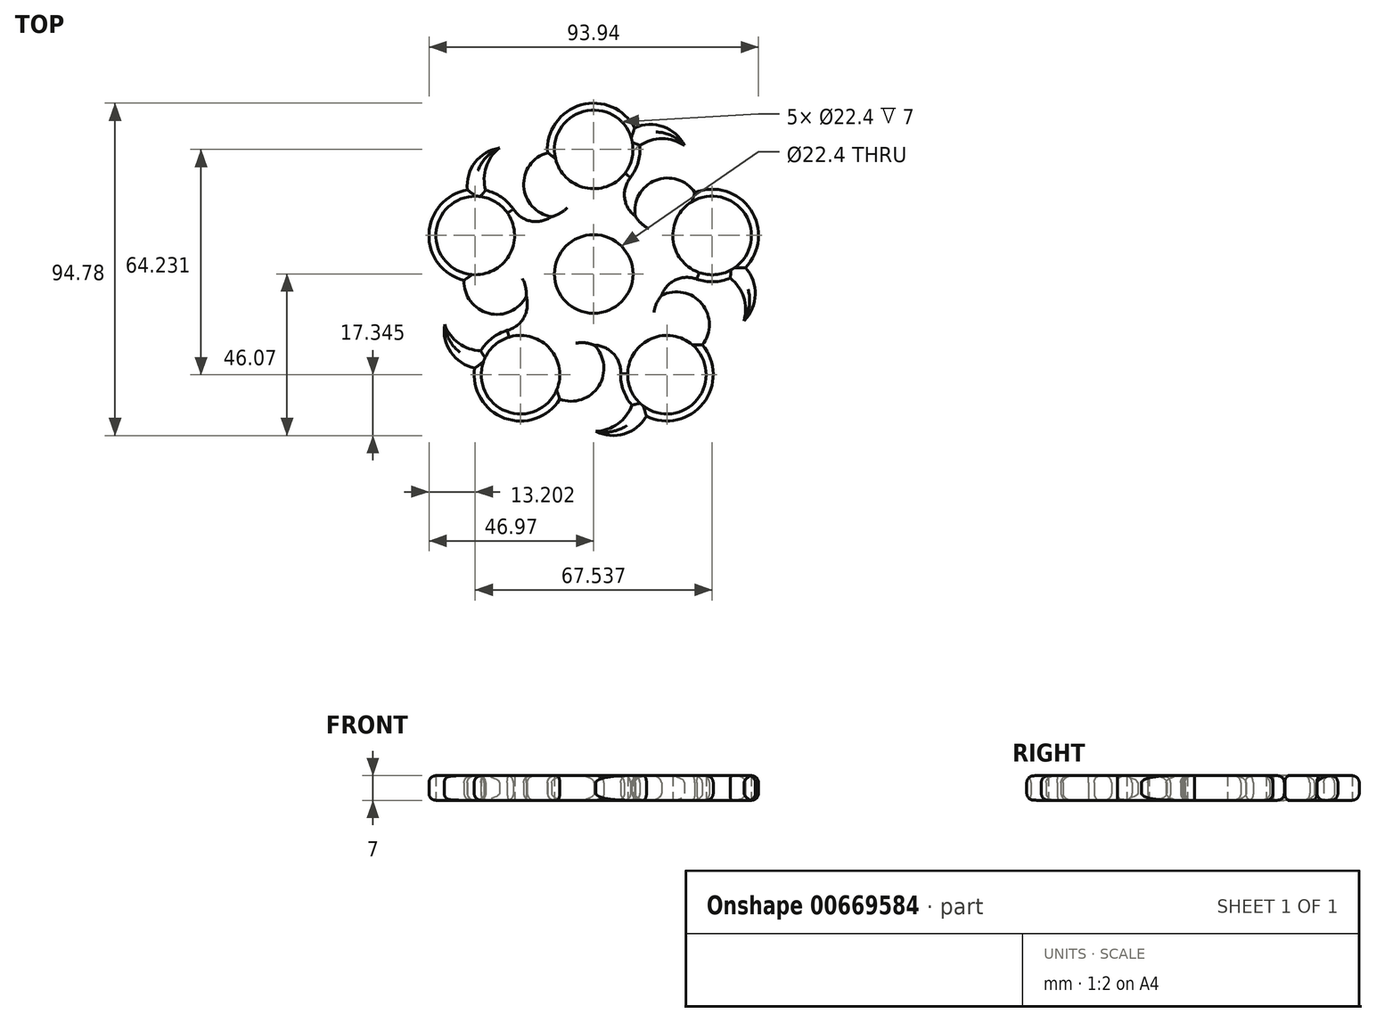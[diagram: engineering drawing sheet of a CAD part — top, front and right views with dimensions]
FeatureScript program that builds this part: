
annotation { "Feature Type Name" : "Feature", "Feature Type Description" : "" }
export const myFeature = defineFeature(function(context is Context, id is Id, definition is map)
    precondition{}
    {
        {
            var Q0;
            Q0=qCreatedBy(makeId("Top.planeOp"),FACE);
            var sketch = newSketch(context, id + "F0", { "sketchPlane" : qUnion([Q0])});
            skCircle(sketch, "E0", {"center": v(0, 0) * mm, "radius": 11.2 * mm});
            skCircle(sketch, "E1", {"center": v(0, 0) * mm, "radius": 13.2 * mm});
            skCircle(sketch, "E2", {"center": v(0, 35.5) * mm, "radius": 11.2 * mm});
            skCircle(sketch, "E3", {"center": v(0, 35.5) * mm, "radius": 13.2 * mm});
            skCircle(sketch, "E4.1.0", {"center": v(-33.77, 10.97) * mm, "radius": 13.2 * mm});
            skCircle(sketch, "E4.1.1", {"center": v(-33.77, 10.97) * mm, "radius": 11.2 * mm});
            skCircle(sketch, "E4.2.0", {"center": v(-20.87, -28.73) * mm, "radius": 13.2 * mm});
            skCircle(sketch, "E4.2.1", {"center": v(-20.87, -28.73) * mm, "radius": 11.2 * mm});
            skCircle(sketch, "E4.3.0", {"center": v(20.87, -28.73) * mm, "radius": 13.2 * mm});
            skCircle(sketch, "E4.3.1", {"center": v(20.87, -28.73) * mm, "radius": 11.2 * mm});
            skCircle(sketch, "E4.4.0", {"center": v(33.77, 10.97) * mm, "radius": 13.2 * mm});
            skCircle(sketch, "E4.4.1", {"center": v(33.77, 10.97) * mm, "radius": 11.2 * mm});
            skArc(sketch, "E5", {"start": v(-22.9, 18.47) * mm, "mid": v(-12.02, 16.34) * mm, "end": v(-10.34, 27.3) * mm});
            skArc(sketch, "E6.1.0", {"start": v(-24.64, -16.08) * mm, "mid": v(-19.26, -6.38) * mm, "end": v(-29.17, -1.4) * mm});
            skArc(sketch, "E6.2.0", {"start": v(7.67, -28.4) * mm, "mid": v(0.12, -20.29) * mm, "end": v(-7.68, -28.17) * mm});
            skArc(sketch, "E6.3.0", {"start": v(29.39, -1.48) * mm, "mid": v(19.33, -6.16) * mm, "end": v(24.42, -16.01) * mm});
            skArc(sketch, "E6.4.0", {"start": v(10.49, 27.5) * mm, "mid": v(11.83, 16.48) * mm, "end": v(22.77, 18.28) * mm});
            skArc(sketch, "E7", {"start": v(28.83, 23.21) * mm, "mid": v(17.62, 26.7) * mm, "end": v(11.83, 16.48) * mm});
            skArc(sketch, "E8.1.0", {"start": v(-13.17, 34.59) * mm, "mid": v(-19.94, 25) * mm, "end": v(-12.02, 16.34) * mm});
            skArc(sketch, "E8.2.0", {"start": v(-36.96, -1.84) * mm, "mid": v(-29.94, -11.24) * mm, "end": v(-19.26, -6.38) * mm});
            skArc(sketch, "E8.3.0", {"start": v(-9.68, -35.72) * mm, "mid": v(1.44, -31.95) * mm, "end": v(0.12, -20.29) * mm});
            skArc(sketch, "E8.4.0", {"start": v(30.98, -20.24) * mm, "mid": v(30.83, -8.5) * mm, "end": v(19.33, -6.16) * mm});
            skArc(sketch, "E9", {"start": v(25.9, 36.65) * mm, "mid": v(19.79, 42) * mm, "end": v(11.68, 41.66) * mm});
            skArc(sketch, "E10", {"start": v(25.9, 36.65) * mm, "mid": v(19.52, 38.6) * mm, "end": v(13.15, 36.65) * mm});
            skArc(sketch, "E11.1.0", {"start": v(-26.85, 35.95) * mm, "mid": v(-33.83, 31.8) * mm, "end": v(-36.01, 23.98) * mm});
            skArc(sketch, "E11.1.1", {"start": v(-26.85, 35.95) * mm, "mid": v(-30.68, 30.5) * mm, "end": v(-30.8, 23.83) * mm});
            skArc(sketch, "E11.2.0", {"start": v(-42.49, -14.43) * mm, "mid": v(-40.7, -22.35) * mm, "end": v(-33.94, -26.84) * mm});
            skArc(sketch, "E11.2.1", {"start": v(-42.49, -14.43) * mm, "mid": v(-38.48, -19.75) * mm, "end": v(-32.18, -21.92) * mm});
            skArc(sketch, "E11.3.0", {"start": v(0.6, -44.87) * mm, "mid": v(8.68, -45.61) * mm, "end": v(15.04, -40.57) * mm});
            skArc(sketch, "E11.3.1", {"start": v(0.6, -44.87) * mm, "mid": v(6.9, -42.7) * mm, "end": v(10.9, -37.38) * mm});
            skArc(sketch, "E11.4.0", {"start": v(42.86, -13.3) * mm, "mid": v(46.06, -5.84) * mm, "end": v(43.23, 1.77) * mm});
            skArc(sketch, "E11.4.1", {"start": v(42.86, -13.3) * mm, "mid": v(42.74, -6.64) * mm, "end": v(38.92, -1.18) * mm});
            skSolve(sketch);
        }
        {
            var Q0;
            Q0=makeQuery(id+"F0.imprint","IMPRINT",FACE,{"disambiguationData":[TD([[makeQuery(id+"F0.imprint","IMPRINT",EDGE,{"derivedFrom":sQuery(id+"F0.wireOp",EDGE,"E1")}),-1.0]])]});
            var Q1;
            Q1=makeQuery(id+"F0.imprint","IMPRINT",FACE,{"disambiguationData":[TD([[makeQuery(id+"F0.imprint","IMPRINT",EDGE,{"derivedFrom":sQuery(id+"F0.wireOp",EDGE,"E0")}),-1.0]])]});
            var Q2;
            {var subQ3=sQuery(id+"F0.wireOp",EDGE,"E7");Q2=makeQuery(id+"F0.imprint","IMPRINT",FACE,{"disambiguationData":[TD([[makeQuery(id+"F0.imprint","IMPRINT",EDGE,{"derivedFrom":subQ3}),1.0]])]});}
            var Q3;
            {var subQ3=sQuery(id+"F0.wireOp",EDGE,"E8.1.0");Q3=makeQuery(id+"F0.imprint","IMPRINT",FACE,{"disambiguationData":[TD([[makeQuery(id+"F0.imprint","IMPRINT",EDGE,{"derivedFrom":subQ3}),1.0]])]});}
            var Q4;
            {var subQ3=sQuery(id+"F0.wireOp",EDGE,"E8.2.0");Q4=makeQuery(id+"F0.imprint","IMPRINT",FACE,{"disambiguationData":[TD([[makeQuery(id+"F0.imprint","IMPRINT",EDGE,{"derivedFrom":subQ3}),1.0]])]});}
            var Q5;
            {var subQ3=sQuery(id+"F0.wireOp",EDGE,"E8.3.0");Q5=makeQuery(id+"F0.imprint","IMPRINT",FACE,{"disambiguationData":[TD([[makeQuery(id+"F0.imprint","IMPRINT",EDGE,{"derivedFrom":subQ3}),1.0]])]});}
            var Q6;
            {var subQ3=sQuery(id+"F0.wireOp",EDGE,"E8.4.0");Q6=makeQuery(id+"F0.imprint","IMPRINT",FACE,{"disambiguationData":[TD([[makeQuery(id+"F0.imprint","IMPRINT",EDGE,{"derivedFrom":subQ3}),1.0]])]});}
            var Q7;
            {var subQ0=sQuery(id+"F0.wireOp",EDGE,"E11.4.0");Q7=makeQuery(id+"F0.imprint","IMPRINT",FACE,{"disambiguationData":[TD([[makeQuery(id+"F0.imprint","IMPRINT",EDGE,{"derivedFrom":subQ0}),1.0]])]});}
            var Q8;
            {var subQ0=sQuery(id+"F0.wireOp",EDGE,"E9");Q8=makeQuery(id+"F0.imprint","IMPRINT",FACE,{"disambiguationData":[TD([[makeQuery(id+"F0.imprint","IMPRINT",EDGE,{"derivedFrom":subQ0}),1.0]])]});}
            var Q9;
            {var subQ0=sQuery(id+"F0.wireOp",EDGE,"E11.1.0");Q9=makeQuery(id+"F0.imprint","IMPRINT",FACE,{"disambiguationData":[TD([[makeQuery(id+"F0.imprint","IMPRINT",EDGE,{"derivedFrom":subQ0}),1.0]])]});}
            var Q10;
            Q10=makeQuery(id+"F0.imprint","IMPRINT",FACE,{"disambiguationData":[TD([[makeQuery(id+"F0.imprint","IMPRINT",EDGE,{"derivedFrom":sQuery(id+"F0.wireOp",EDGE,"E4.1.1")}),-1.0]])]});
            var Q11;
            {var subQ0=sQuery(id+"F0.wireOp",EDGE,"E11.2.0");Q11=makeQuery(id+"F0.imprint","IMPRINT",FACE,{"disambiguationData":[TD([[makeQuery(id+"F0.imprint","IMPRINT",EDGE,{"derivedFrom":subQ0}),1.0]])]});}
            var Q12;
            Q12=makeQuery(id+"F0.imprint","IMPRINT",FACE,{"disambiguationData":[TD([[makeQuery(id+"F0.imprint","IMPRINT",EDGE,{"derivedFrom":sQuery(id+"F0.wireOp",EDGE,"E4.2.1")}),-1.0]])]});
            var Q13;
            Q13=makeQuery(id+"F0.imprint","IMPRINT",FACE,{"disambiguationData":[TD([[makeQuery(id+"F0.imprint","IMPRINT",EDGE,{"derivedFrom":sQuery(id+"F0.wireOp",EDGE,"E4.3.1")}),-1.0]])]});
            var Q14;
            Q14=makeQuery(id+"F0.imprint","IMPRINT",FACE,{"disambiguationData":[TD([[makeQuery(id+"F0.imprint","IMPRINT",EDGE,{"derivedFrom":sQuery(id+"F0.wireOp",EDGE,"E4.4.1")}),-1.0]])]});
            var Q15;
            Q15=makeQuery(id+"F0.imprint","IMPRINT",FACE,{"disambiguationData":[TD([[makeQuery(id+"F0.imprint","IMPRINT",EDGE,{"derivedFrom":sQuery(id+"F0.wireOp",EDGE,"E2")}),-1.0]])]});
            var Q16;
            {var subQ0=sQuery(id+"F0.wireOp",EDGE,"E11.3.0");Q16=makeQuery(id+"F0.imprint","IMPRINT",FACE,{"disambiguationData":[TD([[makeQuery(id+"F0.imprint","IMPRINT",EDGE,{"derivedFrom":subQ0}),1.0]])]});}
            extrude(context, id + "F1", {"entities" : qUnion([Q0, Q1, Q2, Q3, Q4, Q5, Q6, Q7, Q8, Q9, Q10, Q11, Q12, Q13, Q14, Q15, Q16]), "depth" : 7 * mm, "offsetDistance" : 25 * mm});
        }
        {
            var Q0;
            Q0=makeQuery(id+"F1.opExtrude","CAP_EDGE",EDGE,{"disambiguationData":[OSD([sQuery(id+"F0.wireOp",EDGE,"E5")])],"isStart":false});
            var Q1;
            {var subQ0=sQuery(id+"F0.wireOp",EDGE,"E4.1.0");Q1=makeQuery(id+"F1.opExtrude","CAP_EDGE",EDGE,{"disambiguationData":[OSD([subQ0]),TDD([makeQuery(id+"F0.imprint","IMPRINT",EDGE,{"disambiguationData":[TD([[makeQuery(id+"F0.imprint","INTERSECT",VERTEX,{"disambiguationData":[OD(0.0)],"derivedFrom":[subQ0,sQuery(id+"F0.wireOp",EDGE,"E5")]}),-1.0]])],"derivedFrom":subQ0})])],"isStart":false});}
            var Q2;
            Q2=makeQuery(id+"F1.opExtrude","CAP_EDGE",EDGE,{"disambiguationData":[OSD([sQuery(id+"F0.wireOp",EDGE,"E11.1.1")])],"isStart":false});
            var Q3;
            Q3=makeQuery(id+"F1.opExtrude","CAP_EDGE",EDGE,{"disambiguationData":[OSD([sQuery(id+"F0.wireOp",EDGE,"E11.1.0")])],"isStart":false});
            var Q4;
            {var subQ0=sQuery(id+"F0.wireOp",EDGE,"E4.1.0");Q4=makeQuery(id+"F1.opExtrude","CAP_EDGE",EDGE,{"disambiguationData":[OSD([subQ0]),TDD([makeQuery(id+"F0.imprint","IMPRINT",EDGE,{"disambiguationData":[TD([[makeQuery(id+"F0.imprint","INTERSECT",VERTEX,{"derivedFrom":[subQ0,sQuery(id+"F0.wireOp",EDGE,"E8.2.0")]}),1.0]])],"derivedFrom":subQ0})])],"isStart":false});}
            var Q5;
            Q5=makeQuery(id+"F1.opExtrude","CAP_EDGE",EDGE,{"disambiguationData":[OSD([sQuery(id+"F0.wireOp",EDGE,"E8.2.0")])],"isStart":false});
            var Q6;
            Q6=makeQuery(id+"F1.opExtrude","CAP_EDGE",EDGE,{"disambiguationData":[OSD([sQuery(id+"F0.wireOp",EDGE,"E6.1.0")])],"isStart":false});
            var Q7;
            {var subQ0=sQuery(id+"F0.wireOp",EDGE,"E4.2.0");Q7=makeQuery(id+"F1.opExtrude","CAP_EDGE",EDGE,{"disambiguationData":[OSD([subQ0]),TDD([makeQuery(id+"F0.imprint","IMPRINT",EDGE,{"disambiguationData":[TD([[makeQuery(id+"F0.imprint","INTERSECT",VERTEX,{"disambiguationData":[OD(0.0)],"derivedFrom":[subQ0,sQuery(id+"F0.wireOp",EDGE,"E6.1.0")]}),-1.0]])],"derivedFrom":subQ0})])],"isStart":false});}
            var Q8;
            Q8=makeQuery(id+"F1.opExtrude","CAP_EDGE",EDGE,{"disambiguationData":[OSD([sQuery(id+"F0.wireOp",EDGE,"E11.2.1")])],"isStart":false});
            var Q9;
            {var subQ0=sQuery(id+"F0.wireOp",EDGE,"E4.2.0");Q9=makeQuery(id+"F1.opExtrude","CAP_EDGE",EDGE,{"disambiguationData":[OSD([subQ0]),TDD([makeQuery(id+"F0.imprint","IMPRINT",EDGE,{"disambiguationData":[TD([[makeQuery(id+"F0.imprint","INTERSECT",VERTEX,{"derivedFrom":[subQ0,sQuery(id+"F0.wireOp",EDGE,"E8.3.0")]}),1.0]])],"derivedFrom":subQ0})])],"isStart":false});}
            var Q10;
            Q10=makeQuery(id+"F1.opExtrude","CAP_EDGE",EDGE,{"disambiguationData":[OSD([sQuery(id+"F0.wireOp",EDGE,"E11.2.0")])],"isStart":false});
            var Q11;
            Q11=makeQuery(id+"F1.opExtrude","CAP_EDGE",EDGE,{"disambiguationData":[OSD([sQuery(id+"F0.wireOp",EDGE,"E8.3.0")])],"isStart":false});
            var Q12;
            {var subQ0=sQuery(id+"F0.wireOp",EDGE,"E4.3.0");Q12=makeQuery(id+"F1.opExtrude","CAP_EDGE",EDGE,{"disambiguationData":[OSD([subQ0]),TDD([makeQuery(id+"F0.imprint","IMPRINT",EDGE,{"disambiguationData":[TD([[makeQuery(id+"F0.imprint","INTERSECT",VERTEX,{"disambiguationData":[OD(0.0)],"derivedFrom":[subQ0,sQuery(id+"F0.wireOp",EDGE,"E6.2.0")]}),-1.0]])],"derivedFrom":subQ0})])],"isStart":false});}
            var Q13;
            Q13=makeQuery(id+"F1.opExtrude","CAP_EDGE",EDGE,{"disambiguationData":[OSD([sQuery(id+"F0.wireOp",EDGE,"E6.2.0")])],"isStart":false});
            var Q14;
            Q14=makeQuery(id+"F1.opExtrude","CAP_EDGE",EDGE,{"disambiguationData":[OSD([sQuery(id+"F0.wireOp",EDGE,"E11.3.1")])],"isStart":false});
            var Q15;
            Q15=makeQuery(id+"F1.opExtrude","CAP_EDGE",EDGE,{"disambiguationData":[OSD([sQuery(id+"F0.wireOp",EDGE,"E11.3.0")])],"isStart":false});
            var Q16;
            {var subQ0=sQuery(id+"F0.wireOp",EDGE,"E4.3.0");Q16=makeQuery(id+"F1.opExtrude","CAP_EDGE",EDGE,{"disambiguationData":[OSD([subQ0]),TDD([makeQuery(id+"F0.imprint","IMPRINT",EDGE,{"disambiguationData":[TD([[makeQuery(id+"F0.imprint","INTERSECT",VERTEX,{"derivedFrom":[subQ0,sQuery(id+"F0.wireOp",EDGE,"E8.4.0")]}),1.0]])],"derivedFrom":subQ0})])],"isStart":false});}
            var Q17;
            Q17=makeQuery(id+"F1.opExtrude","CAP_EDGE",EDGE,{"disambiguationData":[OSD([sQuery(id+"F0.wireOp",EDGE,"E8.4.0")])],"isStart":false});
            var Q18;
            Q18=makeQuery(id+"F1.opExtrude","CAP_EDGE",EDGE,{"disambiguationData":[OSD([sQuery(id+"F0.wireOp",EDGE,"E6.3.0")])],"isStart":false});
            var Q19;
            {var subQ0=sQuery(id+"F0.wireOp",EDGE,"E4.4.0");Q19=makeQuery(id+"F1.opExtrude","CAP_EDGE",EDGE,{"disambiguationData":[OSD([subQ0]),TDD([makeQuery(id+"F0.imprint","IMPRINT",EDGE,{"disambiguationData":[TD([[makeQuery(id+"F0.imprint","INTERSECT",VERTEX,{"disambiguationData":[OD(0.0)],"derivedFrom":[subQ0,sQuery(id+"F0.wireOp",EDGE,"E6.3.0")]}),-1.0]])],"derivedFrom":subQ0})])],"isStart":false});}
            var Q20;
            Q20=makeQuery(id+"F1.opExtrude","CAP_EDGE",EDGE,{"disambiguationData":[OSD([sQuery(id+"F0.wireOp",EDGE,"E11.4.1")])],"isStart":false});
            var Q21;
            Q21=makeQuery(id+"F1.opExtrude","CAP_EDGE",EDGE,{"disambiguationData":[OSD([sQuery(id+"F0.wireOp",EDGE,"E11.4.0")])],"isStart":false});
            var Q22;
            {var subQ0=sQuery(id+"F0.wireOp",EDGE,"E4.4.0");Q22=makeQuery(id+"F1.opExtrude","CAP_EDGE",EDGE,{"disambiguationData":[OSD([subQ0]),TDD([makeQuery(id+"F0.imprint","IMPRINT",EDGE,{"disambiguationData":[TD([[makeQuery(id+"F0.imprint","INTERSECT",VERTEX,{"derivedFrom":[subQ0,sQuery(id+"F0.wireOp",EDGE,"E7")]}),1.0]])],"derivedFrom":subQ0})])],"isStart":false});}
            var Q23;
            Q23=makeQuery(id+"F1.opExtrude","CAP_EDGE",EDGE,{"disambiguationData":[OSD([sQuery(id+"F0.wireOp",EDGE,"E7")])],"isStart":false});
            var Q24;
            Q24=makeQuery(id+"F1.opExtrude","CAP_EDGE",EDGE,{"disambiguationData":[OSD([sQuery(id+"F0.wireOp",EDGE,"E6.4.0")])],"isStart":false});
            var Q25;
            {var subQ0=sQuery(id+"F0.wireOp",EDGE,"E3");Q25=makeQuery(id+"F1.opExtrude","CAP_EDGE",EDGE,{"disambiguationData":[OSD([subQ0]),TDD([makeQuery(id+"F0.imprint","IMPRINT",EDGE,{"disambiguationData":[TD([[makeQuery(id+"F0.imprint","INTERSECT",VERTEX,{"disambiguationData":[OD(0.0)],"derivedFrom":[subQ0,sQuery(id+"F0.wireOp",EDGE,"E6.4.0")]}),-1.0]])],"derivedFrom":subQ0})])],"isStart":false});}
            var Q26;
            Q26=makeQuery(id+"F1.opExtrude","CAP_EDGE",EDGE,{"disambiguationData":[OSD([sQuery(id+"F0.wireOp",EDGE,"E10")])],"isStart":false});
            var Q27;
            Q27=makeQuery(id+"F1.opExtrude","CAP_EDGE",EDGE,{"disambiguationData":[OSD([sQuery(id+"F0.wireOp",EDGE,"E9")])],"isStart":false});
            var Q28;
            {var subQ0=sQuery(id+"F0.wireOp",EDGE,"E3");Q28=makeQuery(id+"F1.opExtrude","CAP_EDGE",EDGE,{"disambiguationData":[OSD([subQ0]),TDD([makeQuery(id+"F0.imprint","IMPRINT",EDGE,{"disambiguationData":[TD([[makeQuery(id+"F0.imprint","INTERSECT",VERTEX,{"derivedFrom":[subQ0,sQuery(id+"F0.wireOp",EDGE,"E8.1.0")]}),1.0]])],"derivedFrom":subQ0})])],"isStart":false});}
            var Q29;
            Q29=makeQuery(id+"F1.opExtrude","CAP_EDGE",EDGE,{"disambiguationData":[OSD([sQuery(id+"F0.wireOp",EDGE,"E8.1.0")])],"isStart":false});
            fillet(context, id + "F2", {"entities" : qUnion([Q0, Q1, Q2, Q3, Q4, Q5, Q6, Q7, Q8, Q9, Q10, Q11, Q12, Q13, Q14, Q15, Q16, Q17, Q18, Q19, Q20, Q21, Q22, Q23, Q24, Q25, Q26, Q27, Q28, Q29]), "radius" : 2 * mm, "tangentPropagation" : true, "allowEdgeOverflow" : false});
        }
        {
            var Q0;
            Q0=makeQuery(id+"F1.opExtrude","CAP_EDGE",EDGE,{"disambiguationData":[OSD([sQuery(id+"F0.wireOp",EDGE,"E8.3.0")])],"isStart":true});
            var Q1;
            {var subQ0=sQuery(id+"F0.wireOp",EDGE,"E4.2.0");Q1=makeQuery(id+"F1.opExtrude","CAP_EDGE",EDGE,{"disambiguationData":[OSD([subQ0]),TDD([makeQuery(id+"F0.imprint","IMPRINT",EDGE,{"disambiguationData":[TD([[makeQuery(id+"F0.imprint","INTERSECT",VERTEX,{"derivedFrom":[subQ0,sQuery(id+"F0.wireOp",EDGE,"E8.3.0")]}),1.0]])],"derivedFrom":subQ0})])],"isStart":true});}
            var Q2;
            Q2=makeQuery(id+"F1.opExtrude","CAP_EDGE",EDGE,{"disambiguationData":[OSD([sQuery(id+"F0.wireOp",EDGE,"E11.2.0")])],"isStart":true});
            var Q3;
            Q3=makeQuery(id+"F1.opExtrude","CAP_EDGE",EDGE,{"disambiguationData":[OSD([sQuery(id+"F0.wireOp",EDGE,"E6.1.0")])],"isStart":true});
            var Q4;
            {var subQ0=sQuery(id+"F0.wireOp",EDGE,"E4.2.0");Q4=makeQuery(id+"F1.opExtrude","CAP_EDGE",EDGE,{"disambiguationData":[OSD([subQ0]),TDD([makeQuery(id+"F0.imprint","IMPRINT",EDGE,{"disambiguationData":[TD([[makeQuery(id+"F0.imprint","INTERSECT",VERTEX,{"disambiguationData":[OD(0.0)],"derivedFrom":[subQ0,sQuery(id+"F0.wireOp",EDGE,"E6.1.0")]}),-1.0]])],"derivedFrom":subQ0})])],"isStart":true});}
            var Q5;
            Q5=makeQuery(id+"F1.opExtrude","CAP_EDGE",EDGE,{"disambiguationData":[OSD([sQuery(id+"F0.wireOp",EDGE,"E11.2.1")])],"isStart":true});
            var Q6;
            Q6=makeQuery(id+"F1.opExtrude","CAP_EDGE",EDGE,{"disambiguationData":[OSD([sQuery(id+"F0.wireOp",EDGE,"E8.2.0")])],"isStart":true});
            var Q7;
            {var subQ0=sQuery(id+"F0.wireOp",EDGE,"E4.1.0");Q7=makeQuery(id+"F1.opExtrude","CAP_EDGE",EDGE,{"disambiguationData":[OSD([subQ0]),TDD([makeQuery(id+"F0.imprint","IMPRINT",EDGE,{"disambiguationData":[TD([[makeQuery(id+"F0.imprint","INTERSECT",VERTEX,{"derivedFrom":[subQ0,sQuery(id+"F0.wireOp",EDGE,"E8.2.0")]}),1.0]])],"derivedFrom":subQ0})])],"isStart":true});}
            var Q8;
            Q8=makeQuery(id+"F1.opExtrude","CAP_EDGE",EDGE,{"disambiguationData":[OSD([sQuery(id+"F0.wireOp",EDGE,"E11.1.0")])],"isStart":true});
            var Q9;
            {var subQ0=sQuery(id+"F0.wireOp",EDGE,"E4.1.0");Q9=makeQuery(id+"F1.opExtrude","CAP_EDGE",EDGE,{"disambiguationData":[OSD([subQ0]),TDD([makeQuery(id+"F0.imprint","IMPRINT",EDGE,{"disambiguationData":[TD([[makeQuery(id+"F0.imprint","INTERSECT",VERTEX,{"disambiguationData":[OD(0.0)],"derivedFrom":[subQ0,sQuery(id+"F0.wireOp",EDGE,"E5")]}),-1.0]])],"derivedFrom":subQ0})])],"isStart":true});}
            var Q10;
            Q10=makeQuery(id+"F1.opExtrude","CAP_EDGE",EDGE,{"disambiguationData":[OSD([sQuery(id+"F0.wireOp",EDGE,"E11.1.1")])],"isStart":true});
            var Q11;
            Q11=makeQuery(id+"F1.opExtrude","CAP_EDGE",EDGE,{"disambiguationData":[OSD([sQuery(id+"F0.wireOp",EDGE,"E5")])],"isStart":true});
            var Q12;
            Q12=makeQuery(id+"F1.opExtrude","CAP_EDGE",EDGE,{"disambiguationData":[OSD([sQuery(id+"F0.wireOp",EDGE,"E8.1.0")])],"isStart":true});
            var Q13;
            {var subQ0=sQuery(id+"F0.wireOp",EDGE,"E3");Q13=makeQuery(id+"F1.opExtrude","CAP_EDGE",EDGE,{"disambiguationData":[OSD([subQ0]),TDD([makeQuery(id+"F0.imprint","IMPRINT",EDGE,{"disambiguationData":[TD([[makeQuery(id+"F0.imprint","INTERSECT",VERTEX,{"derivedFrom":[subQ0,sQuery(id+"F0.wireOp",EDGE,"E8.1.0")]}),1.0]])],"derivedFrom":subQ0})])],"isStart":true});}
            var Q14;
            Q14=makeQuery(id+"F1.opExtrude","CAP_EDGE",EDGE,{"disambiguationData":[OSD([sQuery(id+"F0.wireOp",EDGE,"E9")])],"isStart":true});
            var Q15;
            Q15=makeQuery(id+"F1.opExtrude","CAP_EDGE",EDGE,{"disambiguationData":[OSD([sQuery(id+"F0.wireOp",EDGE,"E6.4.0")])],"isStart":true});
            var Q16;
            {var subQ0=sQuery(id+"F0.wireOp",EDGE,"E3");Q16=makeQuery(id+"F1.opExtrude","CAP_EDGE",EDGE,{"disambiguationData":[OSD([subQ0]),TDD([makeQuery(id+"F0.imprint","IMPRINT",EDGE,{"disambiguationData":[TD([[makeQuery(id+"F0.imprint","INTERSECT",VERTEX,{"disambiguationData":[OD(0.0)],"derivedFrom":[subQ0,sQuery(id+"F0.wireOp",EDGE,"E6.4.0")]}),-1.0]])],"derivedFrom":subQ0})])],"isStart":true});}
            var Q17;
            {var subQ0=sQuery(id+"F0.wireOp",EDGE,"E3");Q17=makeQuery(id+"F1.opExtrude","CAP_EDGE",EDGE,{"disambiguationData":[OSD([subQ0]),TDD([makeQuery(id+"F0.imprint","IMPRINT",EDGE,{"disambiguationData":[TD([[makeQuery(id+"F0.imprint","INTERSECT",VERTEX,{"disambiguationData":[OD(0.0)],"derivedFrom":[subQ0,sQuery(id+"F0.wireOp",EDGE,"E6.4.0")]}),-1.0]])],"derivedFrom":subQ0})])],"isStart":true});}
            var Q18;
            Q18=makeQuery(id+"F1.opExtrude","CAP_EDGE",EDGE,{"disambiguationData":[OSD([sQuery(id+"F0.wireOp",EDGE,"E7")])],"isStart":true});
            var Q19;
            {var subQ0=sQuery(id+"F0.wireOp",EDGE,"E4.4.0");Q19=makeQuery(id+"F1.opExtrude","CAP_EDGE",EDGE,{"disambiguationData":[OSD([subQ0]),TDD([makeQuery(id+"F0.imprint","IMPRINT",EDGE,{"disambiguationData":[TD([[makeQuery(id+"F0.imprint","INTERSECT",VERTEX,{"derivedFrom":[subQ0,sQuery(id+"F0.wireOp",EDGE,"E7")]}),1.0]])],"derivedFrom":subQ0})])],"isStart":true});}
            var Q20;
            Q20=makeQuery(id+"F1.opExtrude","CAP_EDGE",EDGE,{"disambiguationData":[OSD([sQuery(id+"F0.wireOp",EDGE,"E11.4.0")])],"isStart":true});
            var Q21;
            Q21=makeQuery(id+"F1.opExtrude","CAP_EDGE",EDGE,{"disambiguationData":[OSD([sQuery(id+"F0.wireOp",EDGE,"E6.3.0")])],"isStart":true});
            var Q22;
            Q22=makeQuery(id+"F1.opExtrude","CAP_EDGE",EDGE,{"disambiguationData":[OSD([sQuery(id+"F0.wireOp",EDGE,"E11.4.1")])],"isStart":true});
            var Q23;
            {var subQ0=sQuery(id+"F0.wireOp",EDGE,"E4.4.0");Q23=makeQuery(id+"F1.opExtrude","CAP_EDGE",EDGE,{"disambiguationData":[OSD([subQ0]),TDD([makeQuery(id+"F0.imprint","IMPRINT",EDGE,{"disambiguationData":[TD([[makeQuery(id+"F0.imprint","INTERSECT",VERTEX,{"disambiguationData":[OD(0.0)],"derivedFrom":[subQ0,sQuery(id+"F0.wireOp",EDGE,"E6.3.0")]}),-1.0]])],"derivedFrom":subQ0})])],"isStart":true});}
            var Q24;
            Q24=makeQuery(id+"F1.opExtrude","CAP_EDGE",EDGE,{"disambiguationData":[OSD([sQuery(id+"F0.wireOp",EDGE,"E8.4.0")])],"isStart":true});
            var Q25;
            {var subQ0=sQuery(id+"F0.wireOp",EDGE,"E4.3.0");Q25=makeQuery(id+"F1.opExtrude","CAP_EDGE",EDGE,{"disambiguationData":[OSD([subQ0]),TDD([makeQuery(id+"F0.imprint","IMPRINT",EDGE,{"disambiguationData":[TD([[makeQuery(id+"F0.imprint","INTERSECT",VERTEX,{"derivedFrom":[subQ0,sQuery(id+"F0.wireOp",EDGE,"E8.4.0")]}),1.0]])],"derivedFrom":subQ0})])],"isStart":true});}
            var Q26;
            Q26=makeQuery(id+"F1.opExtrude","CAP_EDGE",EDGE,{"disambiguationData":[OSD([sQuery(id+"F0.wireOp",EDGE,"E11.3.0")])],"isStart":true});
            var Q27;
            Q27=makeQuery(id+"F1.opExtrude","CAP_EDGE",EDGE,{"disambiguationData":[OSD([sQuery(id+"F0.wireOp",EDGE,"E11.3.1")])],"isStart":true});
            var Q28;
            Q28=makeQuery(id+"F1.opExtrude","CAP_EDGE",EDGE,{"disambiguationData":[OSD([sQuery(id+"F0.wireOp",EDGE,"E6.2.0")])],"isStart":true});
            var Q29;
            {var subQ0=sQuery(id+"F0.wireOp",EDGE,"E4.3.0");Q29=makeQuery(id+"F1.opExtrude","CAP_EDGE",EDGE,{"disambiguationData":[OSD([subQ0]),TDD([makeQuery(id+"F0.imprint","IMPRINT",EDGE,{"disambiguationData":[TD([[makeQuery(id+"F0.imprint","INTERSECT",VERTEX,{"disambiguationData":[OD(0.0)],"derivedFrom":[subQ0,sQuery(id+"F0.wireOp",EDGE,"E6.2.0")]}),-1.0]])],"derivedFrom":subQ0})])],"isStart":true});}
            fillet(context, id + "F3", {"entities" : qUnion([Q0, Q1, Q2, Q3, Q4, Q5, Q6, Q7, Q8, Q9, Q10, Q11, Q12, Q13, Q14, Q15, Q16, Q17, Q18, Q19, Q20, Q21, Q22, Q23, Q24, Q25, Q26, Q27, Q28, Q29]), "radius" : 2 * mm, "tangentPropagation" : true, "allowEdgeOverflow" : false});
        }
    });
